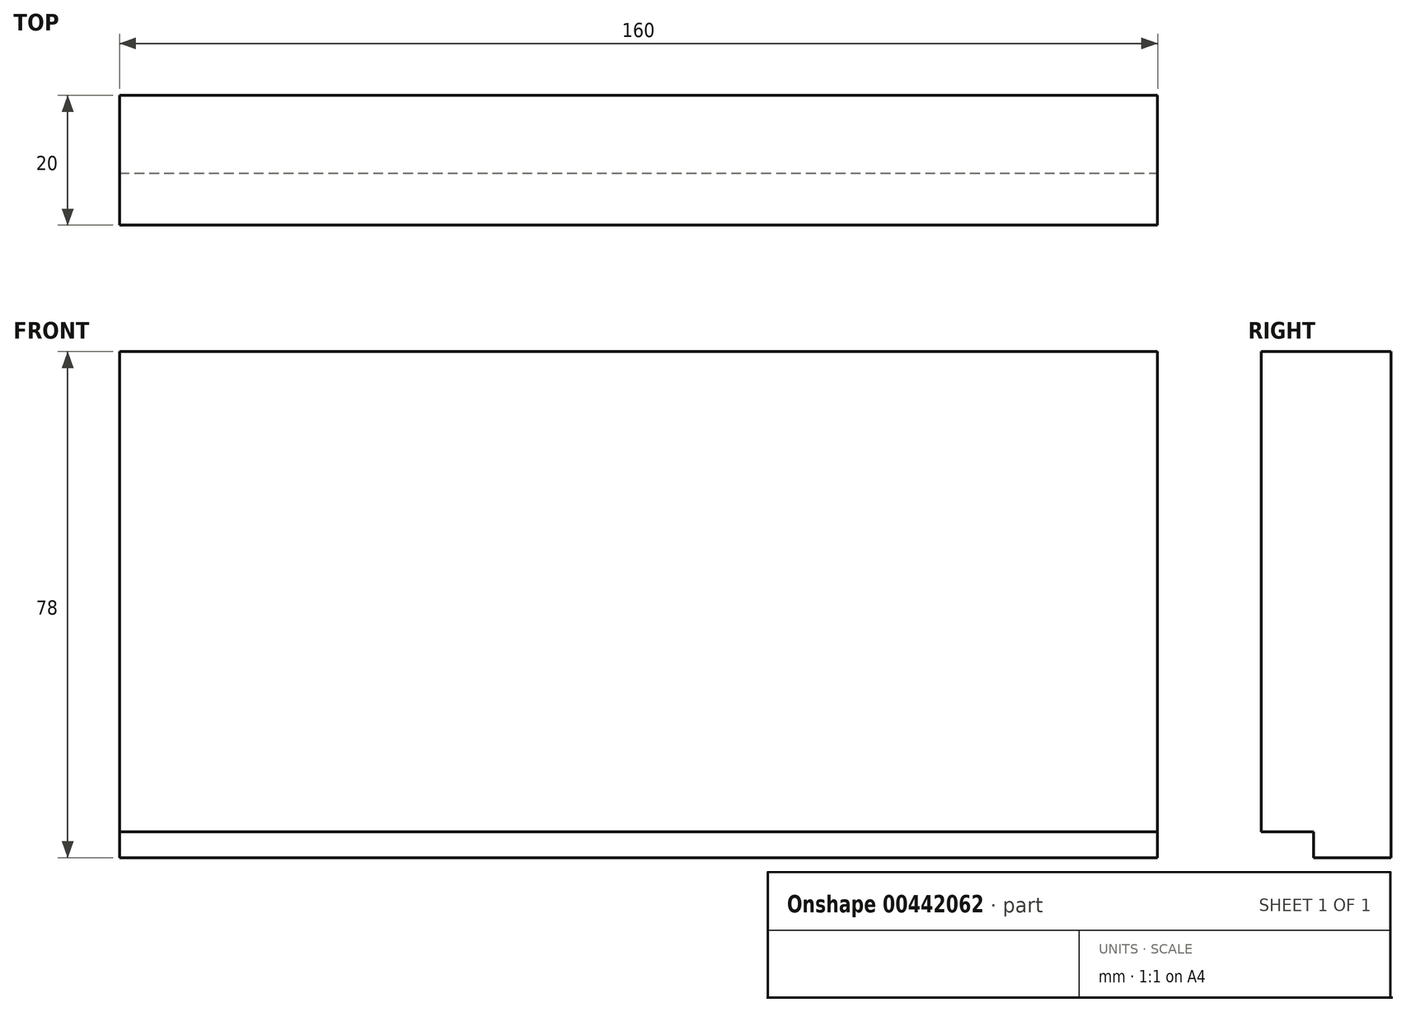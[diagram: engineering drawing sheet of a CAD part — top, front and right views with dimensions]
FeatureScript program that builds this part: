
annotation { "Feature Type Name" : "Feature", "Feature Type Description" : "" }
export const myFeature = defineFeature(function(context is Context, id is Id, definition is map)
    precondition{}
    {
        {
            var Q0;
            Q0=qCreatedBy(makeId("Front.planeOp"),FACE);
            var sketch = newSketch(context, id + "F0", { "sketchPlane" : qUnion([Q0])});
            skLineSegment(sketch, "E0.bottom", {"start": v(-86.33, 35.78) * mm, "end": v(73.67, 35.78) * mm});
            skLineSegment(sketch, "E0.top", {"start": v(-86.33, -42.22) * mm, "end": v(73.67, -42.22) * mm});
            skLineSegment(sketch, "E0.left", {"start": v(-86.33, 35.78) * mm, "end": v(-86.33, -42.22) * mm});
            skLineSegment(sketch, "E0.right", {"start": v(73.67, 35.78) * mm, "end": v(73.67, -42.22) * mm});
            skSolve(sketch);
        }
        {
            var Q0;
            Q0=makeQuery(id+"F0.imprint","IMPRINT",FACE,{"disambiguationData":[TD([[makeQuery(id+"F0.imprint","IMPRINT",EDGE,{"derivedFrom":sQuery(id+"F0.wireOp",EDGE,"E0.bottom")}),-1.0]])]});
            extrude(context, id + "F1", {"entities" : qUnion([Q0]), "depth" : 12 * mm});
        }
        {
            var Q0;
            Q0=makeQuery(id+"F1.opExtrude","CAP_FACE",FACE,{"disambiguationData":[OSD([sQuery(id+"F0.wireOp",EDGE,"E0.bottom"),sQuery(id+"F0.wireOp",EDGE,"E0.top"),sQuery(id+"F0.wireOp",EDGE,"E0.left"),sQuery(id+"F0.wireOp",EDGE,"E0.right")])],"isStart":false});
            var sketch = newSketch(context, id + "F2", { "sketchPlane" : qUnion([Q0])});
            skLineSegment(sketch, "E1.bottom", {"start": v(-86.33, 35.78) * mm, "end": v(73.67, 35.78) * mm});
            skLineSegment(sketch, "E1.top", {"start": v(-86.33, -38.22) * mm, "end": v(73.67, -38.22) * mm});
            skLineSegment(sketch, "E1.left", {"start": v(-86.33, 35.78) * mm, "end": v(-86.33, -38.22) * mm});
            skLineSegment(sketch, "E1.right", {"start": v(73.67, 35.78) * mm, "end": v(73.67, -38.22) * mm});
            skSolve(sketch);
        }
        {
            var Q0;
            Q0 = qSketchRegion(id + "F2", true);
            var Q1;
            Q1 = qSketchRegion(id + "F0", true);
            extrude(context, id + "F3", {"entities" : qUnion([Q0, Q1]), "operationType" : NewBodyOperationType.ADD, "depth" : 8 * mm});
        }
    });
